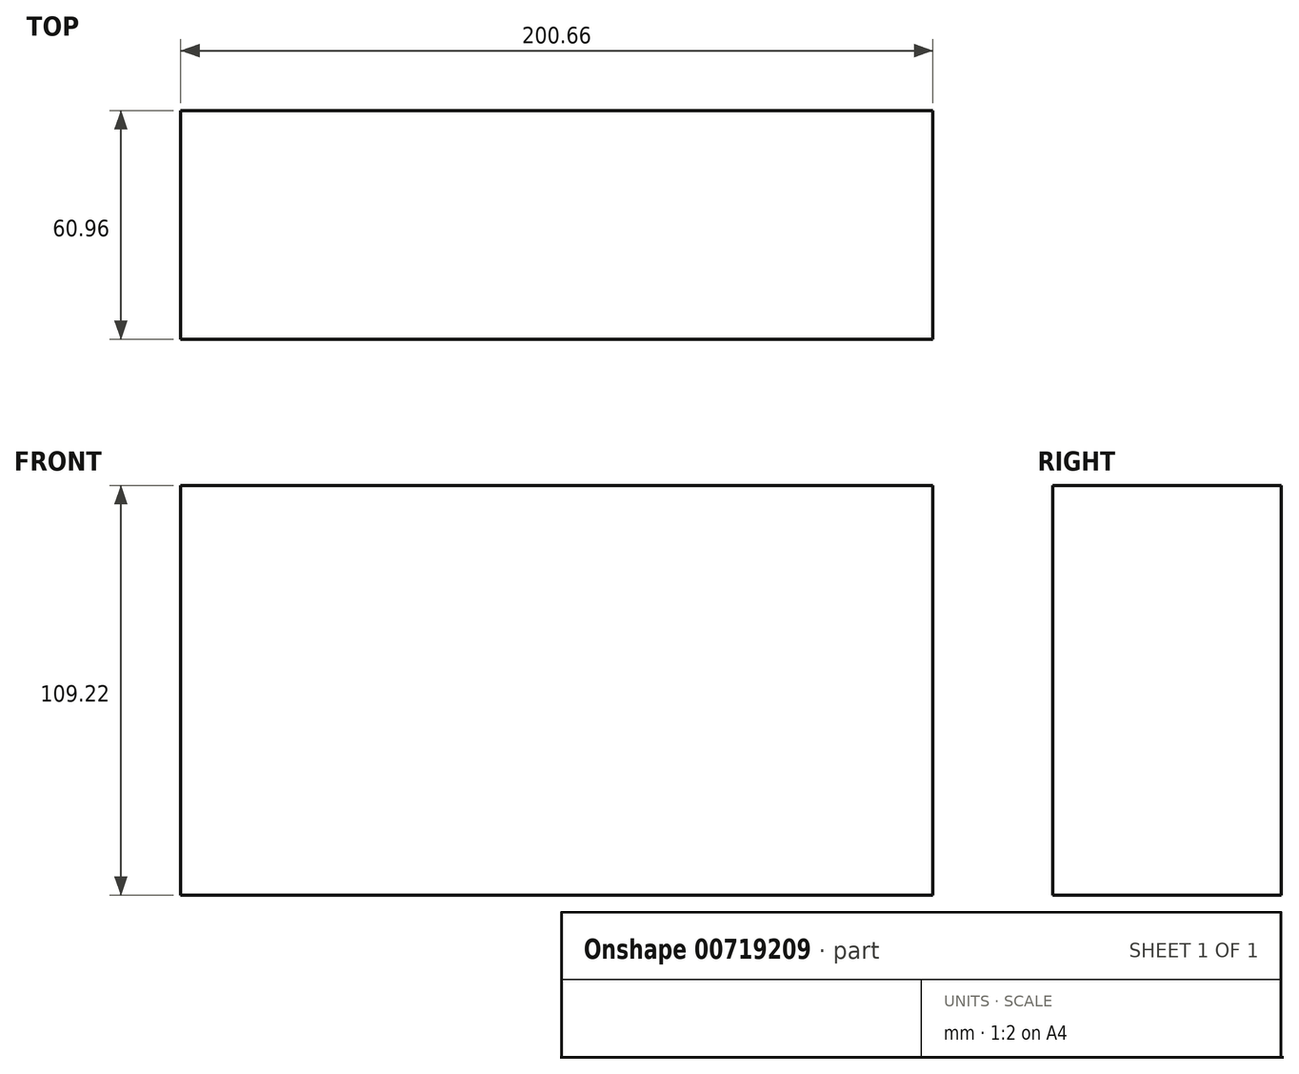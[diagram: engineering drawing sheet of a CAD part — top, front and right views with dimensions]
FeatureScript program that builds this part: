
annotation { "Feature Type Name" : "Feature", "Feature Type Description" : "" }
export const myFeature = defineFeature(function(context is Context, id is Id, definition is map)
    precondition{}
    {
        {
            var Q0;
            Q0=qCreatedBy(makeId("Top.planeOp"),FACE);
            var sketch = newSketch(context, id + "F0", { "sketchPlane" : qUnion([Q0])});
            skLineSegment(sketch, "E0.bottom", {"start": v(100.33, -30.48) * mm, "end": v(-100.33, -30.48) * mm});
            skLineSegment(sketch, "E0.top", {"start": v(100.33, 30.48) * mm, "end": v(-100.33, 30.48) * mm});
            skLineSegment(sketch, "E0.left", {"start": v(100.33, -30.48) * mm, "end": v(100.33, 30.48) * mm});
            skLineSegment(sketch, "E0.right", {"start": v(-100.33, -30.48) * mm, "end": v(-100.33, 30.48) * mm});
            skPoint(sketch, "E0.middle", {"position": v(0, 0) * mm});
            skSolve(sketch);
        }
        {
            var Q0;
            Q0=makeQuery(id+"F0.imprint","IMPRINT",FACE,{"disambiguationData":[TD([[makeQuery(id+"F0.imprint","IMPRINT",EDGE,{"derivedFrom":sQuery(id+"F0.wireOp",EDGE,"E0.bottom")}),-1.0]])]});
            extrude(context, id + "F1", {"entities" : qUnion([Q0]), "depth" : 109.22 * mm, "offsetDistance" : 25.4 * mm});
        }
    });
